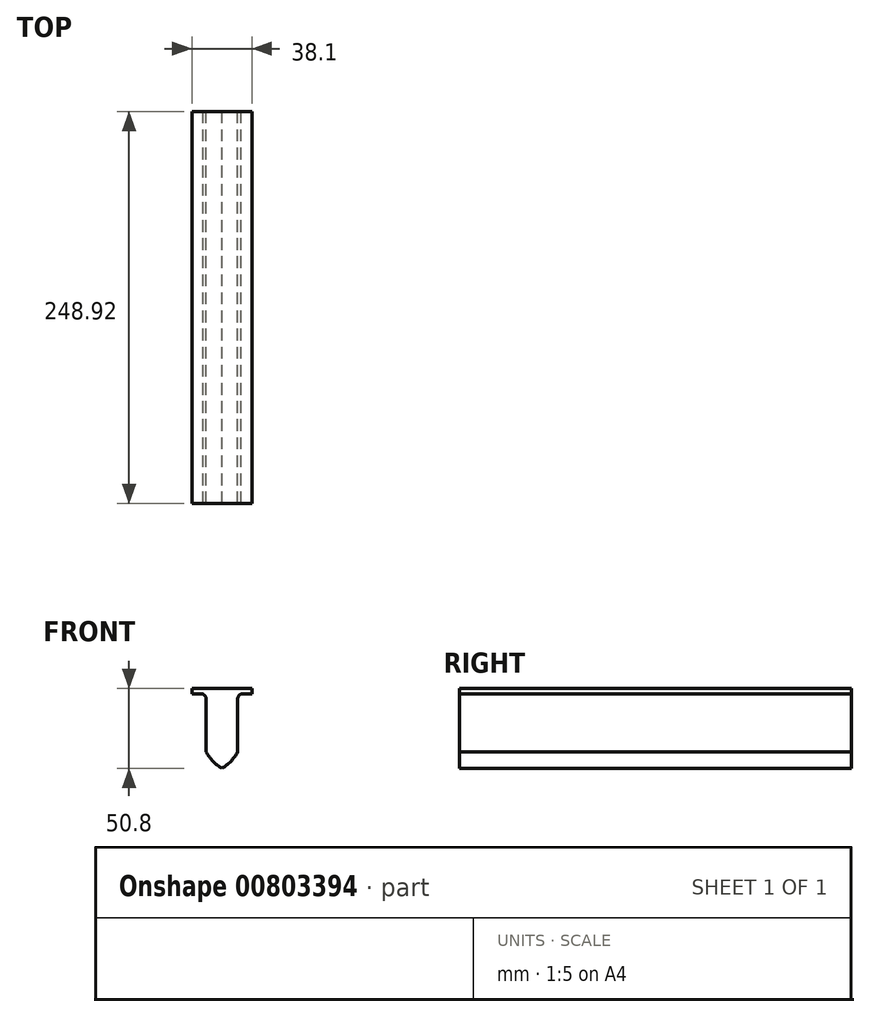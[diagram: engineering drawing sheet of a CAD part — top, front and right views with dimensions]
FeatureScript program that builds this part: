
annotation { "Feature Type Name" : "Feature", "Feature Type Description" : "" }
export const myFeature = defineFeature(function(context is Context, id is Id, definition is map)
    precondition{}
    {
        {
            var Q0;
            Q0=qCreatedBy(makeId("Front.planeOp"),FACE);
            var sketch = newSketch(context, id + "F0", { "sketchPlane" : qUnion([Q0])});
            skLineSegment(sketch, "E0.bottom", {"start": v(-19.05, 25.4) * mm, "end": v(19.05, 25.4) * mm});
            skLineSegment(sketch, "E0.left", {"start": v(-19.05, 25.4) * mm, "end": v(-19.05, 21.86) * mm});
            skLineSegment(sketch, "E0.right", {"start": v(19.05, 25.4) * mm, "end": v(19.05, 21.86) * mm});
            skLineSegment(sketch, "E1.left", {"start": v(-10, -15.06) * mm, "end": v(-10, 18.47) * mm});
            skLineSegment(sketch, "E1.right", {"start": v(10, -15.06) * mm, "end": v(10, 18.47) * mm});
            skLineSegment(sketch, "E2", {"start": v(-19.05, 21.86) * mm, "end": v(-12.06, 21.86) * mm});
            skArc(sketch, "E3", {"start": v(-10, 18.47) * mm, "mid": v(-10.55, 20.46) * mm, "end": v(-12.06, 21.86) * mm});
            skArc(sketch, "E4", {"start": v(-10, -15.06) * mm, "mid": v(-5.65, -20.87) * mm, "end": v(0, -25.4) * mm});
            skArc(sketch, "E5.MirrorCS", {"start": v(10, 18.47) * mm, "mid": v(10.55, 20.46) * mm, "end": v(12.06, 21.86) * mm});
            skArc(sketch, "E6.MirrorCS", {"start": v(10, -15.06) * mm, "mid": v(5.65, -20.87) * mm, "end": v(0, -25.4) * mm});
            skLineSegment(sketch, "E7.MirrorCS", {"start": v(19.05, 21.86) * mm, "end": v(12.06, 21.86) * mm});
            skPoint(sketch, "E8.orphan", {"position": v(10, -25.4) * mm});
            skPoint(sketch, "E0.top.start.orphan", {"position": v(-10, -25.4) * mm});
            skSolve(sketch);
        }
        {
            var Q0;
            Q0 = qSketchRegion(id + "F0", true);
            extrude(context, id + "F1", {"entities" : qUnion([Q0]), "depth" : 248.92 * mm, "offsetDistance" : 25.4 * mm});
        }
    });
